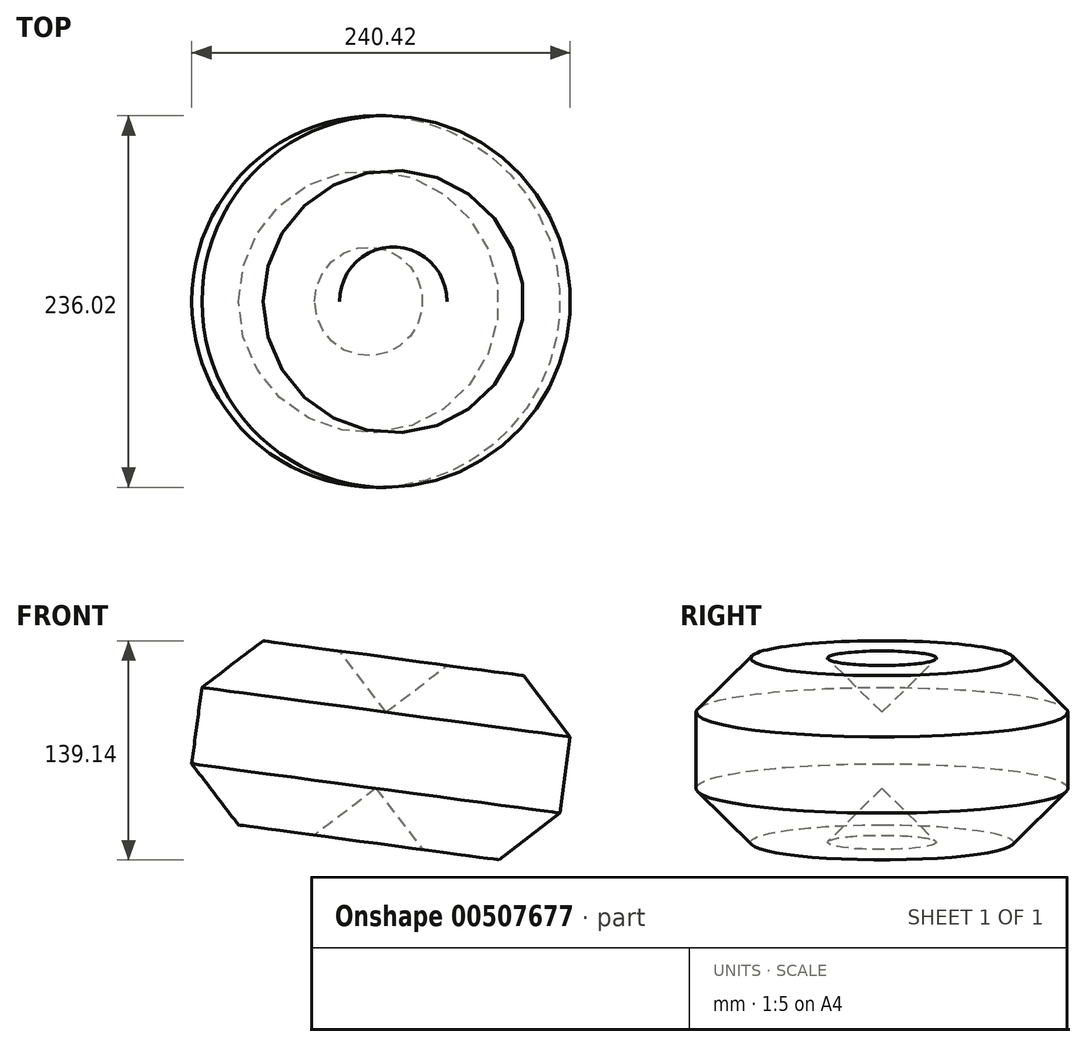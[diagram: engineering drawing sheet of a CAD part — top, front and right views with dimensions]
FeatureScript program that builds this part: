
annotation { "Feature Type Name" : "Feature", "Feature Type Description" : "" }
export const myFeature = defineFeature(function(context is Context, id is Id, definition is map)
    precondition{}
    {
        {
            var Q0;
            Q0=qCreatedBy(makeId("Front.planeOp"),FACE);
            var sketch = newSketch(context, id + "F0", { "sketchPlane" : qUnion([Q0])});
            skCircle(sketch, "E0.cCircle", {"center": v(0, 0) * mm, "radius": 63.87 * mm, "construction": true});
            skLineSegment(sketch, "E0.0", {"start": v(-32.06, -55.23) * mm, "end": v(-61.73, -16.39) * mm});
            skLineSegment(sketch, "E0.1", {"start": v(-61.73, -16.39) * mm, "end": v(-55.23, 32.06) * mm});
            skLineSegment(sketch, "E0.2", {"start": v(-55.23, 32.06) * mm, "end": v(-16.39, 61.73) * mm});
            skLineSegment(sketch, "E0.3", {"start": v(-16.39, 61.73) * mm, "end": v(32.06, 55.23) * mm});
            skLineSegment(sketch, "E0.4", {"start": v(32.06, 55.23) * mm, "end": v(61.73, 16.39) * mm});
            skLineSegment(sketch, "E0.5", {"start": v(61.73, 16.39) * mm, "end": v(55.23, -32.06) * mm});
            skLineSegment(sketch, "E0.6", {"start": v(55.23, -32.06) * mm, "end": v(16.39, -61.73) * mm});
            skLineSegment(sketch, "E0.7", {"start": v(16.39, -61.73) * mm, "end": v(-32.06, -55.23) * mm});
            skSolve(sketch);
        }
        {
            var Q0;
            Q0 = qSketchRegion(id + "F0", true);
            var Q1;
            Q1=sQuery(id+"F0.wireOp",EDGE,"E0.1");
            revolve(context, id + "F1", {"entities" : qUnion([Q0]), "axis" : qUnion([Q1]), "revolveType" : RevolveType.FULL});
        }
    });
